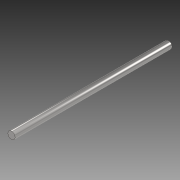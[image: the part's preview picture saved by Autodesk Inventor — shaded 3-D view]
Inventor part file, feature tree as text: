
AUTODESK INVENTOR PART (.ipt)
format: ipt  version: 2020 (Build 240168000, 168)  size: 81,920 bytes
history: native  units: mm
features: extrude x1, sketch x1
ambient origin geometry x8: Origin, YZ Plane, XZ Plane, XY Plane, X Axis, Y Axis, Z Axis, Center Point
bodies: Solid1 (feature_tree)
feature tree (2):
  extrude  "Extrusion1"  Depth=206.0mm TaperAngle=0.0deg
  sketch  "Sketch1"  dims[d0=9.525mm d1=206.0mm d2=0.0mm]
